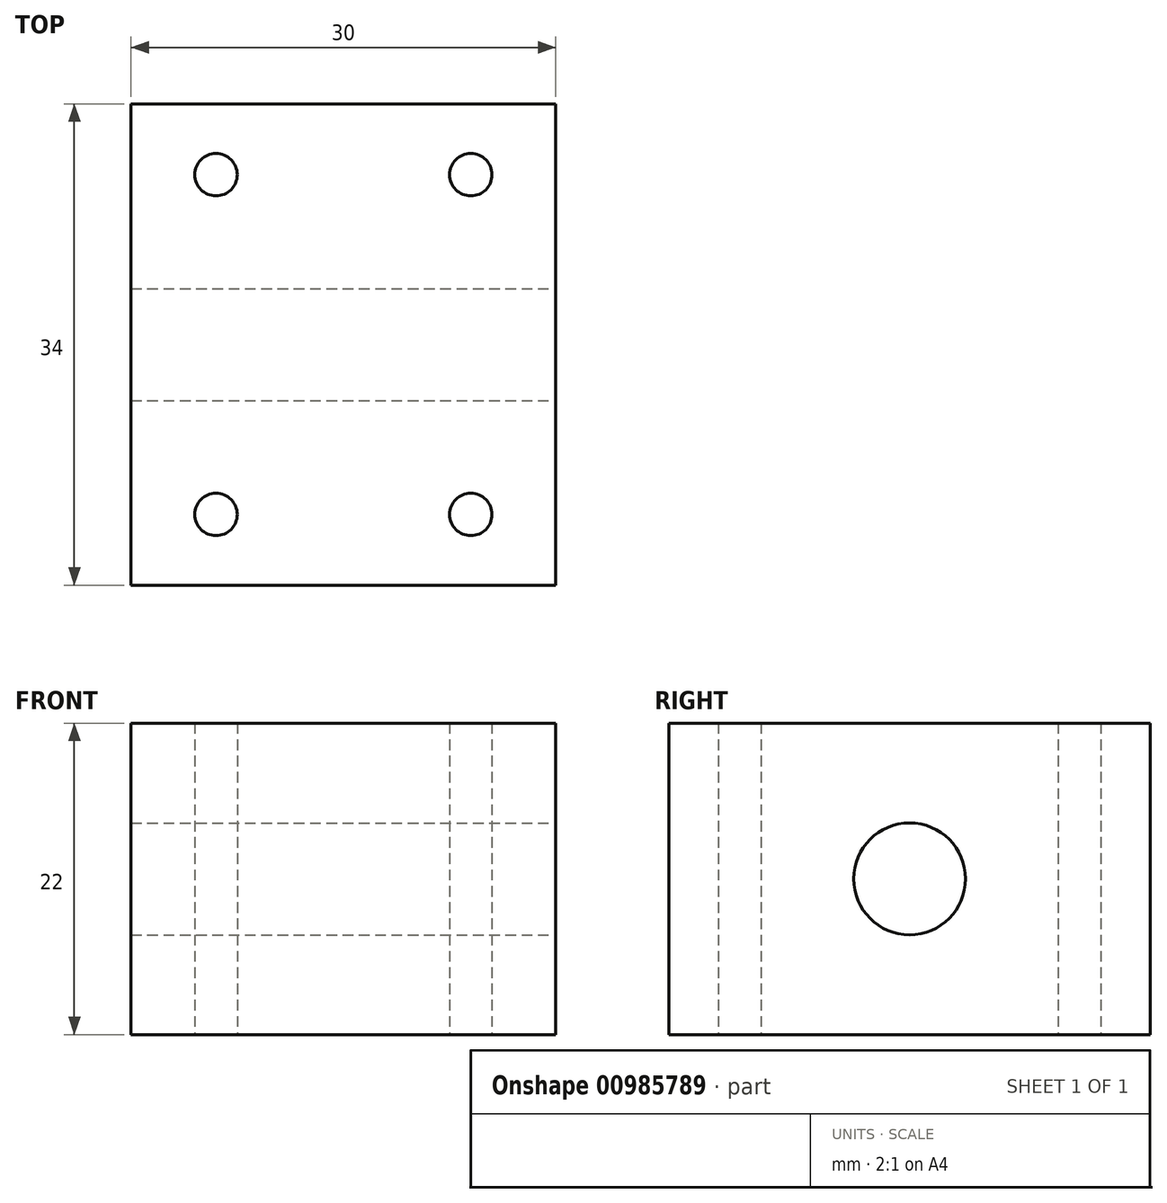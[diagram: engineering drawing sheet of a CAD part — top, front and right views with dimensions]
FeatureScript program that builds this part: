
annotation { "Feature Type Name" : "Feature", "Feature Type Description" : "" }
export const myFeature = defineFeature(function(context is Context, id is Id, definition is map)
    precondition{}
    {
        {
            var Q0;
            Q0=qCreatedBy(makeId("Top.planeOp"),FACE);
            var sketch = newSketch(context, id + "F0", { "sketchPlane" : qUnion([Q0])});
            skLineSegment(sketch, "E0.bottom", {"start": v(0, 0) * mm, "end": v(-30, 0) * mm});
            skLineSegment(sketch, "E0.top", {"start": v(0, 34) * mm, "end": v(-30, 34) * mm});
            skLineSegment(sketch, "E0.left", {"start": v(0, 0) * mm, "end": v(0, 34) * mm});
            skLineSegment(sketch, "E0.right", {"start": v(-30, 0) * mm, "end": v(-30, 34) * mm});
            skCircle(sketch, "E1", {"center": v(-24, 29) * mm, "radius": 1.5 * mm});
            skCircle(sketch, "E2", {"center": v(-6, 29) * mm, "radius": 1.5 * mm});
            skCircle(sketch, "E3", {"center": v(-6, 5) * mm, "radius": 1.5 * mm});
            skCircle(sketch, "E4", {"center": v(-24, 5) * mm, "radius": 1.5 * mm});
            skSolve(sketch);
        }
        {
            var Q0;
            Q0 = qSketchRegion(id + "F0", true);
            extrude(context, id + "F1", {"entities" : qUnion([Q0]), "depth" : 22 * mm, "offsetDistance" : 25 * mm});
        }
        {
            var Q0;
            Q0=makeQuery(id+"F1.opExtrude","SWEPT_FACE",FACE,{"disambiguationData":[OSD([sQuery(id+"F0.wireOp",EDGE,"E0.left")])]});
            var sketch = newSketch(context, id + "F2", { "sketchPlane" : qUnion([Q0])});
            skLineSegment(sketch, "E5.0.0", {"start": v(0, 0) * mm, "end": v(34, 0) * mm});
            skLineSegment(sketch, "E5.0.1", {"start": v(34, 0) * mm, "end": v(34, 22) * mm});
            skLineSegment(sketch, "E5.0.2", {"start": v(34, 22) * mm, "end": v(0, 22) * mm});
            skLineSegment(sketch, "E5.0.3", {"start": v(0, 22) * mm, "end": v(0, 0) * mm});
            skCircle(sketch, "E6", {"center": v(17, 11) * mm, "radius": 3.95 * mm});
            skSolve(sketch);
        }
        {
            var Q0;
            Q0=makeQuery(id+"F2.imprint","IMPRINT",FACE,{"disambiguationData":[TD([[makeQuery(id+"F2.imprint","IMPRINT",EDGE,{"derivedFrom":sQuery(id+"F2.wireOp",EDGE,"E6")}),1.0]])]});
            extrude(context, id + "F3", {"entities" : qUnion([Q0]), "operationType" : NewBodyOperationType.REMOVE, "oppositeDirection" : true, "depth" : 32.7 * mm, "offsetDistance" : 25 * mm});
        }
    });
